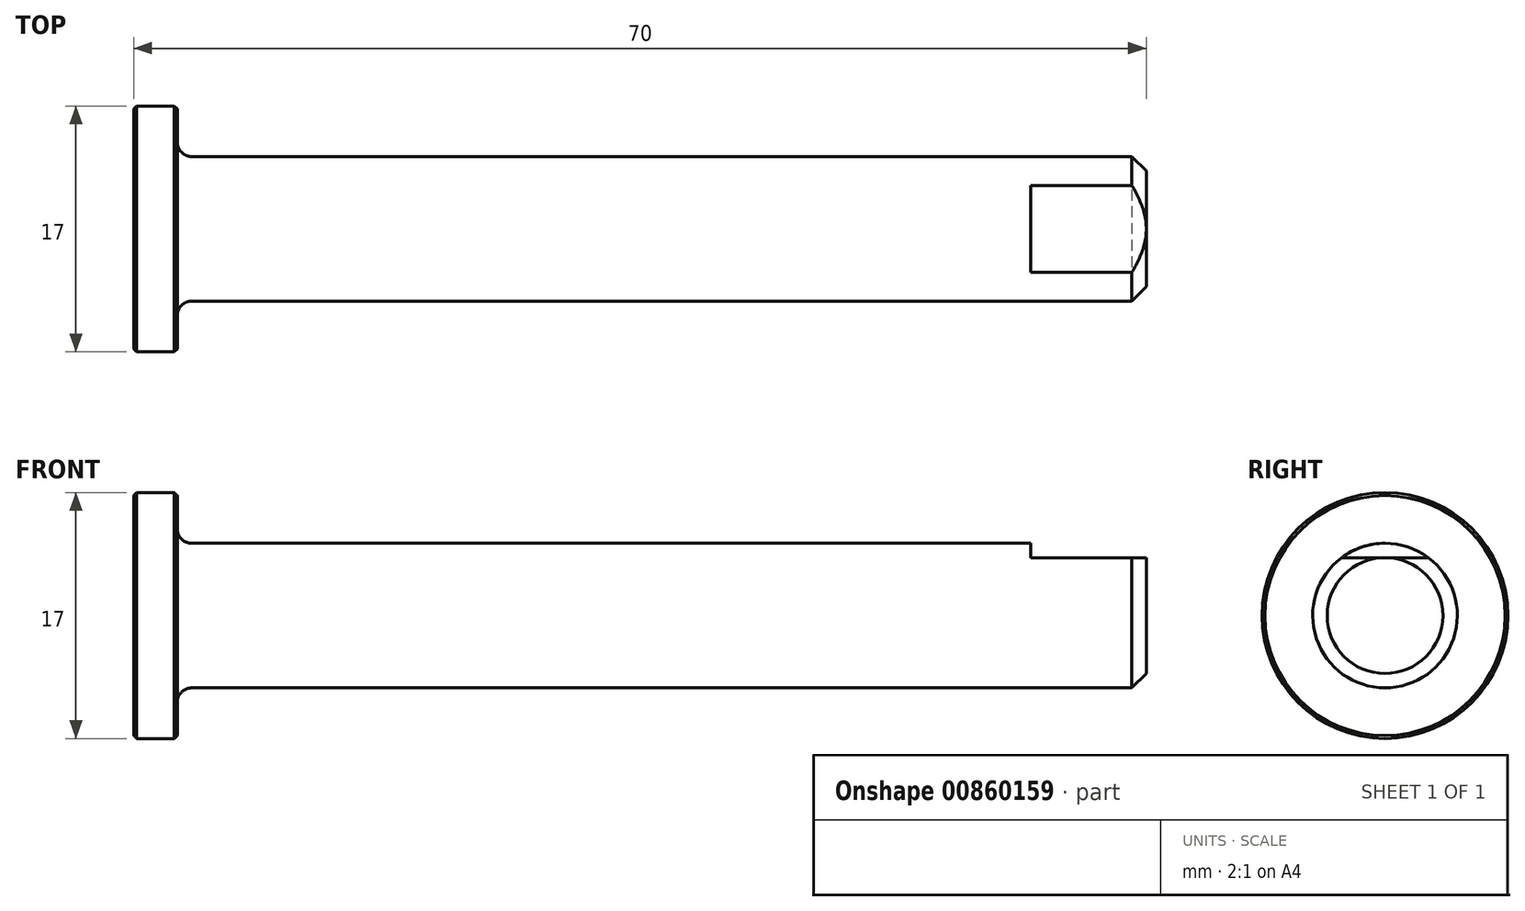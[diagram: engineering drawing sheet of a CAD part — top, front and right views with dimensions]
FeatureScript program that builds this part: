
annotation { "Feature Type Name" : "Feature", "Feature Type Description" : "" }
export const myFeature = defineFeature(function(context is Context, id is Id, definition is map)
    precondition{}
    {
        {
            var Q0;
            Q0=qCreatedBy(makeId("Front.planeOp"),FACE);
            var sketch = newSketch(context, id + "F0", { "sketchPlane" : qUnion([Q0])});
            skLineSegment(sketch, "E0", {"start": v(-3, 0) * mm, "end": v(-3, 8.5) * mm});
            skLineSegment(sketch, "E1", {"start": v(-3, 8.5) * mm, "end": v(0, 8.5) * mm});
            skLineSegment(sketch, "E2", {"start": v(0, 8.5) * mm, "end": v(0, 5) * mm});
            skLineSegment(sketch, "E3", {"start": v(0, 5) * mm, "end": v(67, 5) * mm});
            skLineSegment(sketch, "E4", {"start": v(67, 5) * mm, "end": v(67, 0) * mm});
            skLineSegment(sketch, "E5", {"start": v(67, 0) * mm, "end": v(-3, 0) * mm});
            skSolve(sketch);
        }
        {
            var Q0;
            Q0=makeQuery(id+"F0.imprint","IMPRINT",FACE,{"disambiguationData":[TD([[makeQuery(id+"F0.imprint","IMPRINT",EDGE,{"derivedFrom":sQuery(id+"F0.wireOp",EDGE,"E0")}),-1.0]])]});
            var Q1;
            Q1=sQuery(id+"F0.wireOp",EDGE,"E5");
            revolve(context, id + "F1", {"surfaceOperationType" : NewSurfaceOperationType.NEW, "entities" : qUnion([Q0]), "axis" : qUnion([Q1]), "revolveType" : RevolveType.FULL});
        }
        {
            var Q0;
            Q0=makeQuery(id+"F1.opRevolve","SWEPT_EDGE",EDGE,{"disambiguationData":[OSD([sQuery(id+"F0.wireOp",EDGE,"E1"),sQuery(id+"F0.wireOp",EDGE,"E2")])]});
            var Q1;
            Q1=makeQuery(id+"F1.opRevolve","SWEPT_EDGE",EDGE,{"disambiguationData":[OSD([sQuery(id+"F0.wireOp",EDGE,"E0"),sQuery(id+"F0.wireOp",EDGE,"E1")])]});
            chamfer(context, id + "F2", {"entities" : qUnion([Q0, Q1]), "width" : 0.2 * mm, "tangentPropagation" : true});
        }
        {
            var Q0;
            Q0=makeQuery(id+"F1.opRevolve","SWEPT_EDGE",EDGE,{"disambiguationData":[OSD([sQuery(id+"F0.wireOp",EDGE,"E3"),sQuery(id+"F0.wireOp",EDGE,"E4")])]});
            chamfer(context, id + "F3", {"entities" : qUnion([Q0]), "width" : 1 * mm, "tangentPropagation" : true});
        }
        {
            var Q0;
            Q0=makeQuery(id+"F1.opRevolve","SWEPT_EDGE",EDGE,{"disambiguationData":[OSD([sQuery(id+"F0.wireOp",EDGE,"E2"),sQuery(id+"F0.wireOp",EDGE,"E3")])]});
            fillet(context, id + "F4", {"entities" : qUnion([Q0]), "radius" : 1 * mm, "tangentPropagation" : true, "allowEdgeOverflow" : false});
        }
        {
            var Q0;
            Q0=qCreatedBy(makeId("Front.planeOp"),FACE);
            var sketch = newSketch(context, id + "F5", { "sketchPlane" : qUnion([Q0])});
            skLineSegment(sketch, "E6.bottom", {"start": v(59, 5) * mm, "end": v(67, 5) * mm});
            skLineSegment(sketch, "E6.top", {"start": v(59, 4) * mm, "end": v(67, 4) * mm});
            skLineSegment(sketch, "E6.left", {"start": v(59, 5) * mm, "end": v(59, 4) * mm});
            skLineSegment(sketch, "E6.right", {"start": v(67, 5) * mm, "end": v(67, 4) * mm});
            skSolve(sketch);
        }
        {
            var Q0;
            Q0 = qSketchRegion(id + "F5", true);
            extrude(context, id + "F6", {"entities" : qUnion([Q0]), "operationType" : NewBodyOperationType.REMOVE, "endBound" : BoundingType.SYMMETRIC, "oppositeDirection" : true, "depth" : 25 * mm, "offsetDistance" : 25 * mm});
        }
    });
